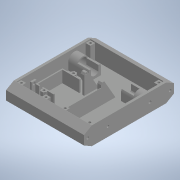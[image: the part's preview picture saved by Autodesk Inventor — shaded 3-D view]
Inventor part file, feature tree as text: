
AUTODESK INVENTOR PART (.ipt)
format: ipt  version: 2020 (Build 240168000, 168)  size: 610,304 bytes
history: native  units: in
note: dims shown in document units (in); Inventor stores cm internally (conversion verified against a paired STEP export)
features: extrude x18, sketch x17, projected_geometry x14, mirror x6, plane x1
ambient origin geometry x8: Origin, YZ Plane, XZ Plane, XY Plane, X Axis, Y Axis, Z Axis, Center Point
bodies: Solid1 (feature_tree)
feature tree (56):
  extrude  "Extrusion1"  Depth=5.9055in
  extrude  "Extrusion2"  TaperAngle=0.0deg  [1 undecoded]
  extrude  "Extrusion3"  Depth=1.063in
  extrude  "Extrusion4"  Depth=0.315in
  extrude  "Extrusion5"  TaperAngle=0.0deg  [1 undecoded]
  extrude  "Extrusion6"  Depth=0.5906in
  mirror  "Mirror1"
  extrude  "Extrusion7"  Depth=0.0787in
  mirror  "Mirror2"
  extrude  "Extrusion8"  Depth=0.6102in
  mirror  "Mirror3"
  plane  "Work Plane1"
  extrude  "Extrusion9"  Depth=0.7874in TaperAngle=0.0deg
  mirror  "Mirror4"
  extrude  "Extrusion10"  Depth=0.1654in TaperAngle=0.0deg
  extrude  "Extrusion11"  Depth=0.1575in
  extrude  "Extrusion12"  TaperAngle=0.0deg  [1 undecoded]
  extrude  "Extrusion13"  Depth=0.2756in
  extrude  "Extrusion14"  Depth=0.4331in
  extrude  "Extrusion17"  Depth=2.7559in
  extrude  "Extrusion18"  Depth=0.0413in
  mirror  "Mirror6"
  extrude  "Extrusion19"  TaperAngle=0.0deg  [1 undecoded]
  mirror  "Mirror7"
  extrude  "Extrusion20"  TaperAngle=60.0deg  [1 undecoded]
  sketch  "Sketch1"  dims[d0=1.1811in d1=5.9055in]
  sketch  "Sketch2"  dims[d2=5.1181in d3=0.0in]
  projected_geometry  "Projected Loop1"
  sketch  "Sketch3"  dims[d4=0.1575in d5=1.063in]
  projected_geometry  "Projected Loop2"
  projected_geometry  "Projected Loop3"
  sketch  "Sketch4"  dims[d6=0.0in d8=0.315in]
  projected_geometry  "Projected Loop4"
  sketch  "Sketch6"  dims[d10=0.993in d11=0.0in]
  sketch  "Sketch7"  dims[d12=0.6496in d13=0.5906in]
  sketch  "Sketch9"  dims[d14=1.5748in d15=0.0787in]
  sketch  "Sketch10"  dims[d16=0.5512in d17=0.0in d18=0.6102in]
  sketch  "Sketch12"  dims[d19=0.4803in d20=0.7874in d21=0.0in]
  projected_geometry  "Projected Loop6"
  projected_geometry  "Projected Loop7"
  projected_geometry  "Projected Loop8"
  sketch  "Sketch13"  dims[d22=0.1654in d23=6.063in d24=0.0in]
  sketch  "Sketch14"  dims[d25=0.5114in d26=0.1575in]
  sketch  "Sketch15"  dims[d27=1.5748in d28=0.0in d29=0.0in]
  projected_geometry  "Projected Loop15"
  sketch  "Sketch16"  dims[d30=0.1575in d31=0.2756in]
  projected_geometry  "Projected Loop19"
  projected_geometry  "Projected Loop20"
  projected_geometry  "Projected Loop21"
  projected_geometry  "Projected Loop22"
  projected_geometry  "Projected Loop23"
  projected_geometry  "Projected Loop24"
  sketch  "Sketch20"  dims[d32=0.0in d33=0.4331in]
  sketch  "Sketch21"  dims[d34=0.0827in d38=2.7559in]
  sketch  "Sketch22"  dims[d40=0.0413in d41=0.0909in]
  sketch  "Sketch23"  dims[d42=0.2362in d43=0.0in d44=60.0deg d45=0.0787in d46=0.315in d48=0.993in d49=0.0in d53=0.2756in d54=0.0in d55=0.4724in d56=1.2008in d57=1.6142in d58=1.5945in d59=0.0787in d60=0.0787in d62=0.315in d63=0.7677in d64=0.0in d66=0.1476in d67=0.2756in d68=0.0in d69=0.7874in d70=0.2953in d71=0.1181in d72=0.0in d89=0.0157in d90=0.0157in d91=0.1476in d92=0.1476in d96=0.315in d97=0.1575in d98=0.1181in d99=0.0in d102=0.1772in d104=0.3346in d105=135.0deg d106=0.2362in d107=0.0in d108=0.0394in d109=0.0in d110=0.0315in d111=0.0394in d112=0.0in]
note: 5 required parameter values undecoded (feature->parameter linkage not recoverable at this tier; creation-order binding heuristic only, values carry confidence <= 0.55)
